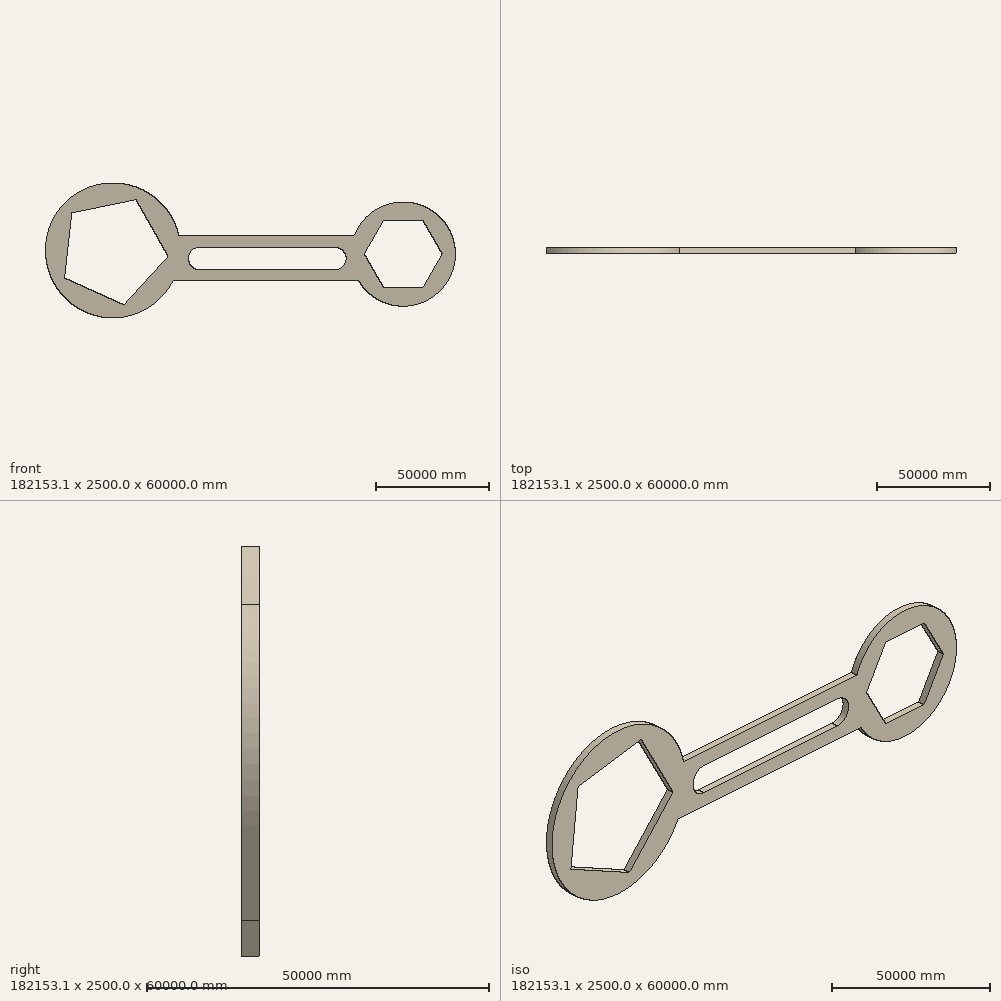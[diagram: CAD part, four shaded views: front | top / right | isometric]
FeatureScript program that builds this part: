
annotation { "Feature Type Name" : "Feature", "Feature Type Description" : "" }
export const myFeature = defineFeature(function(context is Context, id is Id, definition is map)
    precondition{}
    {
        {
            var Q0;
            Q0=qCreatedBy(makeId("Front.planeOp"),FACE);
            var sketch = newSketch(context, id + "F0", { "sketchPlane" : qUnion([Q0])});
            skCircle(sketch, "E0", {"center": v(-32835.05, 34.31) * mm, "radius": 30000 * mm});
            skCircle(sketch, "E1.cCircle", {"center": v(-32835.05, 34.31) * mm, "radius": 20000 * mm, "construction": true});
            skLineSegment(sketch, "E1.0", {"start": v(-8265.72, -2703.12) * mm, "end": v(-27846.16, -24178.42) * mm});
            skLineSegment(sketch, "E1.1", {"start": v(-27846.16, -24178.42) * mm, "end": v(-54321.08, -12192.55) * mm});
            skLineSegment(sketch, "E1.2", {"start": v(-54321.08, -12192.55) * mm, "end": v(-51103.04, 16690.43) * mm});
            skLineSegment(sketch, "E1.3", {"start": v(-51103.04, 16690.43) * mm, "end": v(-22639.26, 22555.22) * mm});
            skLineSegment(sketch, "E1.4", {"start": v(-22639.26, 22555.22) * mm, "end": v(-8265.72, -2703.12) * mm});
            skPoint(sketch, "E1.0.midPoint", {"position": v(-18055.94, -13440.77) * mm});
            skCircle(sketch, "E2", {"center": v(96164.95, -1629.68) * mm, "radius": 23153.1 * mm});
            skCircle(sketch, "E3.cCircle", {"center": v(96164.95, -1629.68) * mm, "radius": 15000 * mm, "construction": true});
            skLineSegment(sketch, "E3.0", {"start": v(104825.2, -16629.68) * mm, "end": v(87504.7, -16629.68) * mm});
            skLineSegment(sketch, "E3.1", {"start": v(87504.7, -16629.68) * mm, "end": v(78844.44, -1629.68) * mm});
            skLineSegment(sketch, "E3.2", {"start": v(78844.44, -1629.68) * mm, "end": v(87504.7, 13370.32) * mm});
            skLineSegment(sketch, "E3.3", {"start": v(87504.7, 13370.32) * mm, "end": v(104825.2, 13370.32) * mm});
            skLineSegment(sketch, "E3.4", {"start": v(104825.2, 13370.32) * mm, "end": v(113485.46, -1629.68) * mm});
            skLineSegment(sketch, "E3.5", {"start": v(113485.46, -1629.68) * mm, "end": v(104825.2, -16629.68) * mm});
            skPoint(sketch, "E3.0.midPoint", {"position": v(96164.95, -16629.68) * mm});
            skPoint(sketch, "E4.2.internal.orphan", {"position": v(198132.78, 0) * mm});
            skLineSegment(sketch, "E5", {"start": v(-3553.22, 6559.23) * mm, "end": v(74508.36, 6559.23) * mm});
            skLineSegment(sketch, "E6", {"start": v(-6031.65, -13440.77) * mm, "end": v(76251.03, -13440.77) * mm});
            skLineSegment(sketch, "E7.left", {"start": v(213004.15, 2900.58) * mm, "end": v(213004.15, 604.47) * mm});
            skLineSegment(sketch, "E7.right", {"start": v(170755.94, 604.47) * mm, "end": v(170755.94, -211.08) * mm});
            skPoint(sketch, "E8.visualSharp", {"position": v(213004.15, 5604.47) * mm});
            skPoint(sketch, "E9.visualSharp", {"position": v(170755.94, 40754.99) * mm});
            skPoint(sketch, "E10.visualSharp", {"position": v(170755.94, -5211.08) * mm});
            skPoint(sketch, "E11.visualSharp", {"position": v(213004.15, -5211.08) * mm});
            skLineSegment(sketch, "E12.bottom", {"start": v(5739.4, 1418.1) * mm, "end": v(65739.4, 1418.1) * mm});
            skLineSegment(sketch, "E12.top", {"start": v(5739.4, -8581.9) * mm, "end": v(65739.4, -8581.9) * mm});
            skLineSegment(sketch, "E12.left", {"start": v(739.4, -3581.9) * mm, "end": v(739.4, -3581.9) * mm});
            skLineSegment(sketch, "E12.right", {"start": v(70739.4, -3581.9) * mm, "end": v(70739.4, -3581.9) * mm});
            skPoint(sketch, "E13.visualSharp", {"position": v(70739.4, 1418.1) * mm});
            skArc(sketch, "E13.filletArc", {"start": v(70739.4, -3581.9) * mm, "mid": v(69274.93, -46.37) * mm, "end": v(65739.4, 1418.1) * mm});
            skPoint(sketch, "E14.visualSharp", {"position": v(739.4, 1418.1) * mm});
            skArc(sketch, "E14.filletArc", {"start": v(5739.4, 1418.1) * mm, "mid": v(2203.86, -46.37) * mm, "end": v(739.4, -3581.9) * mm});
            skPoint(sketch, "E15.visualSharp", {"position": v(739.4, -8581.9) * mm});
            skArc(sketch, "E15.filletArc", {"start": v(739.4, -3581.9) * mm, "mid": v(2203.86, -7117.44) * mm, "end": v(5739.4, -8581.9) * mm});
            skPoint(sketch, "E16.visualSharp", {"position": v(70739.4, -8581.9) * mm});
            skArc(sketch, "E16.filletArc", {"start": v(65739.4, -8581.9) * mm, "mid": v(69274.93, -7117.44) * mm, "end": v(70739.4, -3581.9) * mm});
            skSolve(sketch);
        }
        {
            var Q0;
            Q0 = qSketchRegion(id + "F0", true);
            extrude(context, id + "F1", {"entities" : qUnion([Q0]), "depth" : 2500 * mm, "offsetDistance" : 25 * mm});
        }
    });
